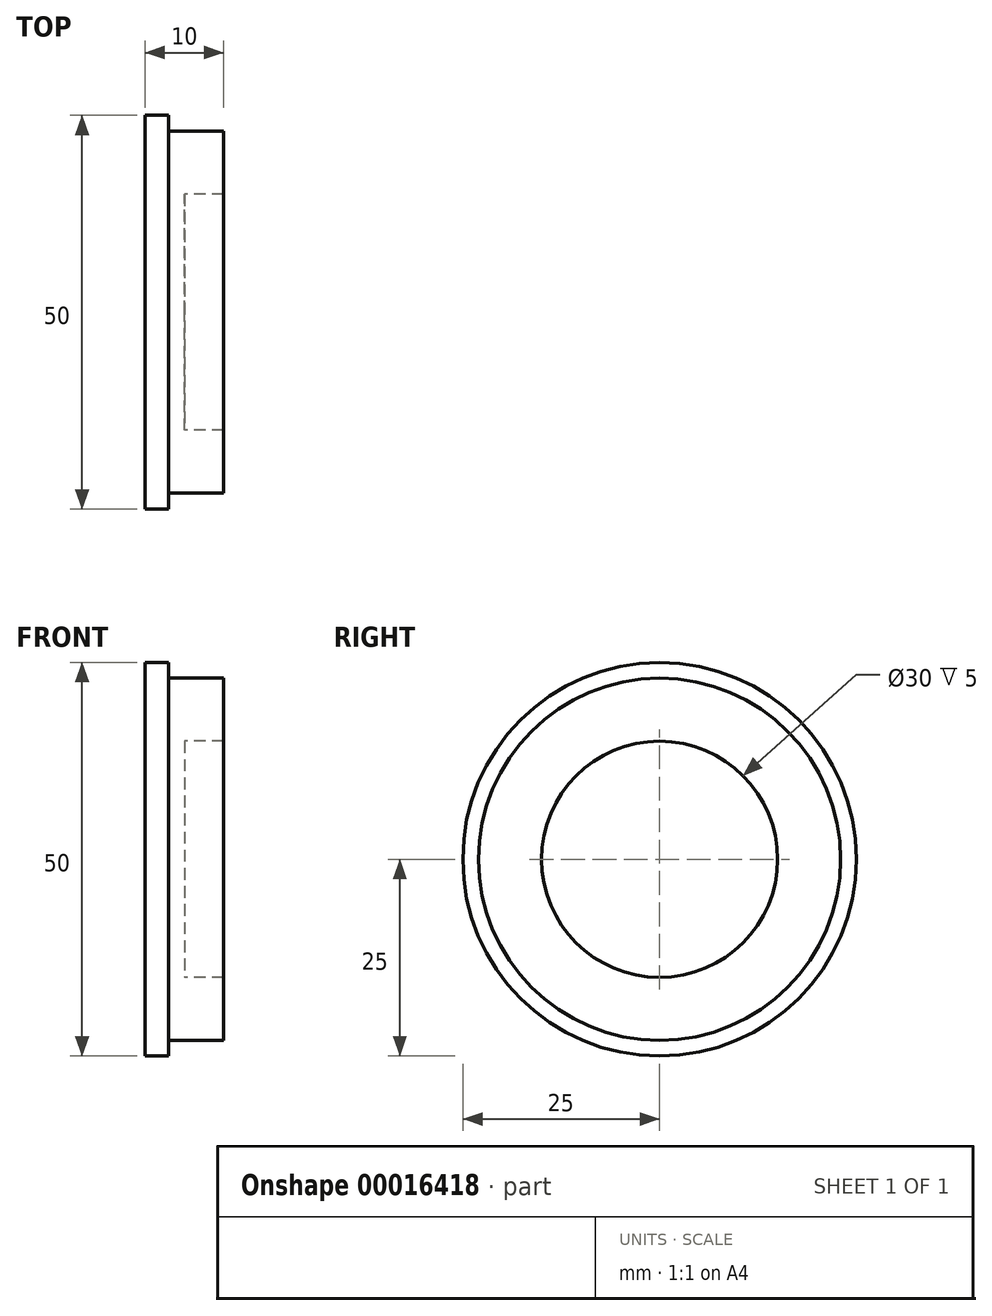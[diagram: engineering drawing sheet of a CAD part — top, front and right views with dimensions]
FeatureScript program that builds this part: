
annotation { "Feature Type Name" : "Feature", "Feature Type Description" : "" }
export const myFeature = defineFeature(function(context is Context, id is Id, definition is map)
    precondition{}
    {
        {
            var Q0;
            Q0=qCreatedBy(makeId("Front.planeOp"),FACE);
            var sketch = newSketch(context, id + "F0", { "sketchPlane" : qUnion([Q0])});
            skLineSegment(sketch, "E0", {"start": v(1, 15) * mm, "end": v(1, 23) * mm});
            skLineSegment(sketch, "E1", {"start": v(1, 23) * mm, "end": v(-6, 23) * mm});
            skLineSegment(sketch, "E2", {"start": v(-6, 23) * mm, "end": v(-6, 25) * mm});
            skLineSegment(sketch, "E3", {"start": v(-6, 25) * mm, "end": v(-9, 25) * mm});
            skLineSegment(sketch, "E4", {"start": v(-9, 25) * mm, "end": v(-9, 0) * mm});
            skLineSegment(sketch, "E5", {"start": v(-9, 0) * mm, "end": v(-4, 0) * mm});
            skLineSegment(sketch, "E6", {"start": v(1, 15) * mm, "end": v(-4, 15) * mm});
            skLineSegment(sketch, "E7", {"start": v(-4, 15) * mm, "end": v(-4, 0) * mm});
            skSolve(sketch);
        }
        {
            var Q0;
            Q0=makeQuery(id+"F0.imprint","IMPRINT",FACE,{"disambiguationData":[TD([[makeQuery(id+"F0.imprint","IMPRINT",EDGE,{"derivedFrom":sQuery(id+"F0.wireOp",EDGE,"E0")}),1.0]])]});
            var Q1;
            Q1=sQuery(id+"F0.wireOp",EDGE,"E5");
            revolve(context, id + "F1", {"entities" : qUnion([Q0]), "axis" : qUnion([Q1]), "revolveType" : RevolveType.FULL});
        }
    });
